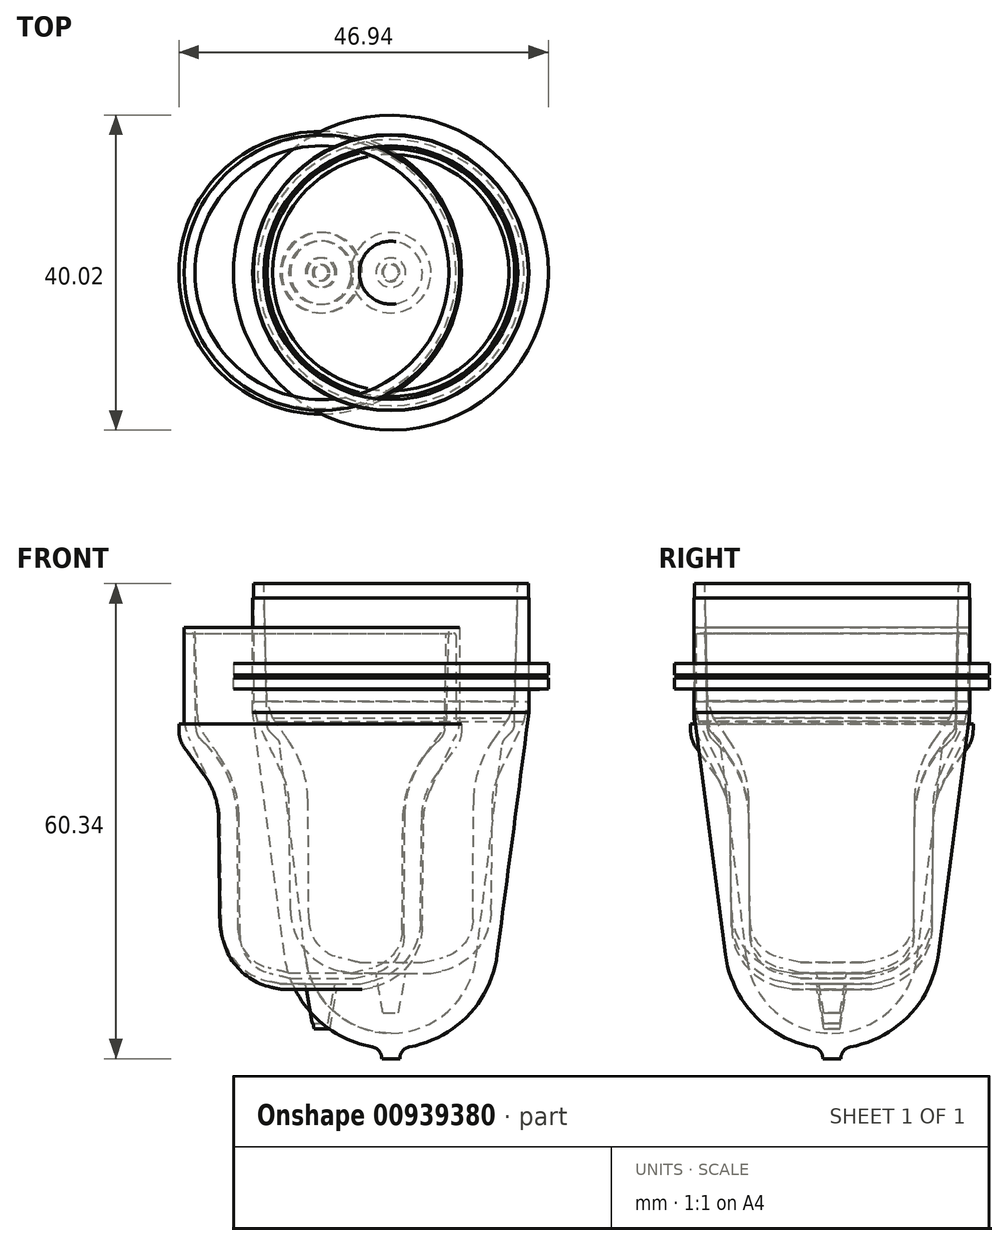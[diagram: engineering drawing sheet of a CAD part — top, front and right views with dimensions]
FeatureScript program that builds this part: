
annotation { "Feature Type Name" : "Feature", "Feature Type Description" : "" }
export const myFeature = defineFeature(function(context is Context, id is Id, definition is map)
    precondition{}
    {
        {
            var Q0;
            Q0=qCreatedBy(makeId("Front.planeOp"),FACE);
            var sketch = newSketch(context, id + "F0", { "sketchPlane" : qUnion([Q0])});
            skLineSegment(sketch, "E0", {"start": v(8.28, 24.33) * mm, "end": v(8.28, 13.23) * mm});
            skLineSegment(sketch, "E1", {"start": v(-7.98, -24.77) * mm, "end": v(-7.1, -19.77) * mm});
            skArc(sketch, "E2", {"start": v(-2.57, -19.48) * mm, "mid": v(1.95, -16.73) * mm, "end": v(3.77, -11.76) * mm});
            skArc(sketch, "E3", {"start": v(5.61, 6.52) * mm, "mid": v(4.38, 4.1) * mm, "end": v(3.94, 1.4) * mm});
            skLineSegment(sketch, "E4", {"start": v(8.98, 13.23) * mm, "end": v(8.98, 12.5) * mm});
            skArc(sketch, "E5", {"start": v(8.23, 10.18) * mm, "mid": v(8.78, 11.29) * mm, "end": v(8.97, 12.5) * mm});
            skLineSegment(sketch, "E6", {"start": v(8.23, 10.18) * mm, "end": v(5.61, 6.52) * mm});
            skLineSegment(sketch, "E7", {"start": v(3.94, 1.4) * mm, "end": v(3.77, -11.76) * mm});
            skLineSegment(sketch, "E8", {"start": v(-2.57, -19.48) * mm, "end": v(-3.98, -19.77) * mm});
            skLineSegment(sketch, "E9", {"start": v(-3.87, -19.75) * mm, "end": v(-3.98, -19.77) * mm});
            skArc(sketch, "E10", {"start": v(8.28, 24.47) * mm, "mid": v(8.2, 24.69) * mm, "end": v(7.98, 24.77) * mm});
            skLineSegment(sketch, "E11", {"start": v(7.98, 24.77) * mm, "end": v(7.33, 24.77) * mm});
            skLineSegment(sketch, "E12", {"start": v(7.03, 24.48) * mm, "end": v(6.82, 12.67) * mm});
            skArc(sketch, "E13", {"start": v(7.33, 24.77) * mm, "mid": v(7.12, 24.69) * mm, "end": v(7.03, 24.48) * mm});
            skLineSegment(sketch, "E14", {"start": v(8.28, 24.47) * mm, "end": v(8.28, 24.32) * mm});
            skLineSegment(sketch, "E15", {"start": v(-8.98, -18.38) * mm, "end": v(-4.98, -18.38) * mm});
            skLineSegment(sketch, "E16", {"start": v(-4.98, -18.38) * mm, "end": v(-2.33, -17.72) * mm});
            skLineSegment(sketch, "E17", {"start": v(6.22, 11.3) * mm, "end": v(5.61, 10.7) * mm});
            skArc(sketch, "E18", {"start": v(6.22, 11.3) * mm, "mid": v(6.66, 11.93) * mm, "end": v(6.82, 12.69) * mm});
            skArc(sketch, "E19", {"start": v(-2.35, -17.72) * mm, "mid": v(0.37, -15.96) * mm, "end": v(1.44, -12.9) * mm});
            skArc(sketch, "E20", {"start": v(5.61, 10.7) * mm, "mid": v(2.65, 6.38) * mm, "end": v(1.55, 1.25) * mm});
            skLineSegment(sketch, "E21", {"start": v(1.51, -1.38) * mm, "end": v(1.44, -12.9) * mm});
            skLineSegment(sketch, "E22", {"start": v(1.55, 1.25) * mm, "end": v(1.51, -1.38) * mm});
            skLineSegment(sketch, "E23", {"start": v(-3.87, -19.75) * mm, "end": v(-7.1, -19.77) * mm});
            skLineSegment(sketch, "E24", {"start": v(-7.98, -24.77) * mm, "end": v(-8.98, -24.77) * mm});
            skLineSegment(sketch, "E25", {"start": v(8.28, 13.23) * mm, "end": v(8.98, 13.23) * mm});
            skLineSegment(sketch, "E26", {"start": v(-8.98, -24.77) * mm, "end": v(-8.98, -18.38) * mm});
            skSolve(sketch);
        }
        {
            var Q0;
            {var subQ7=sQuery(id+"F0.wireOp",EDGE,"E0");Q0=makeQuery(id+"F0.imprint","IMPRINT",FACE,{"disambiguationData":[TD([[makeQuery(id+"F0.imprint","IMPRINT",EDGE,{"derivedFrom":subQ7}),-1.0]])]});}
            var Q1;
            Q1=sQuery(id+"F0.wireOp",EDGE,"E26");
            revolve(context, id + "F1", {"surfaceOperationType" : NewSurfaceOperationType.NEW, "entities" : qUnion([Q0]), "axis" : qUnion([Q1]), "revolveType" : RevolveType.FULL});
        }
        {
            var Q0;
            Q0=qCreatedBy(makeId("Front.planeOp"),FACE);
            var sketch = newSketch(context, id + "F2", { "sketchPlane" : qUnion([Q0])});
            skLineSegment(sketch, "E27", {"start": v(8.75, 25.5) * mm, "end": v(8.75, 14.5) * mm});
            skLineSegment(sketch, "E28", {"start": v(-7.75, -25.5) * mm, "end": v(-6.87, -20.5) * mm});
            skArc(sketch, "E29", {"start": v(-2.35, -20.2) * mm, "mid": v(2.18, -17.45) * mm, "end": v(4, -12.48) * mm});
            skLineSegment(sketch, "E30", {"start": v(8.75, 14.5) * mm, "end": v(8.75, 14.16) * mm});
            skLineSegment(sketch, "E31", {"start": v(4.17, 1.12) * mm, "end": v(4, -12.48) * mm});
            skLineSegment(sketch, "E32", {"start": v(-2.35, -20.2) * mm, "end": v(-3.75, -20.5) * mm});
            skLineSegment(sketch, "E33", {"start": v(-3.65, -20.48) * mm, "end": v(-3.75, -20.5) * mm});
            skLineSegment(sketch, "E34", {"start": v(-8.75, -19.1) * mm, "end": v(-4.75, -19.1) * mm});
            skLineSegment(sketch, "E35", {"start": v(-4.75, -19.1) * mm, "end": v(-2.1, -18.44) * mm});
            skArc(sketch, "E36", {"start": v(-2.12, -18.45) * mm, "mid": v(0.6, -16.69) * mm, "end": v(1.67, -13.63) * mm});
            skLineSegment(sketch, "E37", {"start": v(1.74, -2.1) * mm, "end": v(1.67, -13.63) * mm});
            skLineSegment(sketch, "E38", {"start": v(1.8, 1.53) * mm, "end": v(1.74, -2.1) * mm});
            skLineSegment(sketch, "E39", {"start": v(-3.65, -20.48) * mm, "end": v(-6.87, -20.5) * mm});
            skLineSegment(sketch, "E40", {"start": v(-7.75, -25.5) * mm, "end": v(-8.75, -25.5) * mm});
            skLineSegment(sketch, "E41", {"start": v(-8.75, -25.5) * mm, "end": v(-8.75, -19.1) * mm});
            skArc(sketch, "E42", {"start": v(5.01, 4.8) * mm, "mid": v(4.4, 3.01) * mm, "end": v(4.17, 1.12) * mm});
            skLineSegment(sketch, "E43", {"start": v(5.01, 4.8) * mm, "end": v(8.19, 11.62) * mm});
            skLineSegment(sketch, "E44", {"start": v(4.23, 9.07) * mm, "end": v(6.36, 12.1) * mm});
            skArc(sketch, "E45", {"start": v(8.19, 11.62) * mm, "mid": v(8.6, 12.86) * mm, "end": v(8.75, 14.16) * mm});
            skArc(sketch, "E46", {"start": v(4.23, 9.07) * mm, "mid": v(2.45, 5.49) * mm, "end": v(1.8, 1.53) * mm});
            skArc(sketch, "E47", {"start": v(6.36, 12.1) * mm, "mid": v(6.88, 13.15) * mm, "end": v(7.08, 14.3) * mm});
            skLineSegment(sketch, "E48", {"start": v(7.08, 14.3) * mm, "end": v(7.38, 25.5) * mm});
            skLineSegment(sketch, "E49", {"start": v(8.75, 25.5) * mm, "end": v(7.38, 25.5) * mm});
            skSolve(sketch);
        }
        {
            var Q0;
            Q0=makeQuery(id+"F2.imprint","IMPRINT",FACE,{"disambiguationData":[TD([[makeQuery(id+"F2.imprint","IMPRINT",EDGE,{"derivedFrom":sQuery(id+"F2.wireOp",EDGE,"E27")}),-1.0]])]});
            var Q1;
            Q1=sQuery(id+"F2.wireOp",EDGE,"E41");
            revolve(context, id + "F3", {"surfaceOperationType" : NewSurfaceOperationType.NEW, "entities" : qUnion([Q0]), "axis" : qUnion([Q1]), "revolveType" : RevolveType.FULL});
        }
        {
            var Q0;
            Q0=qCreatedBy(makeId("Front.planeOp"),FACE);
            var sketch = newSketch(context, id + "F4", { "sketchPlane" : qUnion([Q0])});
            skLineSegment(sketch, "E50", {"start": v(1, -23.46) * mm, "end": v(1.88, -18.46) * mm});
            skArc(sketch, "E51", {"start": v(6.4, -18.16) * mm, "mid": v(10.93, -15.41) * mm, "end": v(12.74, -10.44) * mm});
            skLineSegment(sketch, "E52", {"start": v(12.92, 3.16) * mm, "end": v(12.74, -10.44) * mm});
            skLineSegment(sketch, "E53", {"start": v(6.4, -18.16) * mm, "end": v(5, -18.46) * mm});
            skLineSegment(sketch, "E54", {"start": v(5.1, -18.44) * mm, "end": v(5, -18.46) * mm});
            skLineSegment(sketch, "E55", {"start": v(0, -17.06) * mm, "end": v(4, -17.06) * mm});
            skLineSegment(sketch, "E56", {"start": v(4, -17.06) * mm, "end": v(6.64, -16.4) * mm});
            skArc(sketch, "E57", {"start": v(6.63, -16.4) * mm, "mid": v(9.35, -14.65) * mm, "end": v(10.42, -11.59) * mm});
            skLineSegment(sketch, "E58", {"start": v(10.49, -0.06) * mm, "end": v(10.42, -11.59) * mm});
            skLineSegment(sketch, "E59", {"start": v(10.54, 3.57) * mm, "end": v(10.49, -0.06) * mm});
            skLineSegment(sketch, "E60", {"start": v(5.1, -18.44) * mm, "end": v(1.88, -18.46) * mm});
            skLineSegment(sketch, "E61", {"start": v(1, -23.46) * mm, "end": v(0, -23.46) * mm});
            skLineSegment(sketch, "E62", {"start": v(0, -23.46) * mm, "end": v(0, -17.06) * mm});
            skArc(sketch, "E63", {"start": v(13.76, 6.85) * mm, "mid": v(13.14, 5.05) * mm, "end": v(12.92, 3.16) * mm});
            skArc(sketch, "E64", {"start": v(12.98, 11.1) * mm, "mid": v(11.2, 7.52) * mm, "end": v(10.54, 3.57) * mm});
            skLineSegment(sketch, "E65", {"start": v(-1.16, -27.43) * mm, "end": v(-1.1, -27.43) * mm});
            skLineSegment(sketch, "E66", {"start": v(-1.1, -27.43) * mm, "end": v(-0.81, -27.43) * mm});
            skLineSegment(sketch, "E67", {"start": v(-0.81, -27.43) * mm, "end": v(-0.46, -27.43) * mm});
            skLineSegment(sketch, "E68", {"start": v(-0.46, -27.43) * mm, "end": v(-0.04, -27.43) * mm});
            skLineSegment(sketch, "E69", {"start": v(-0.04, -27.43) * mm, "end": v(0, -27.43) * mm});
            skLineSegment(sketch, "E70", {"start": v(-1.16, -27.36) * mm, "end": v(-1.16, -27.43) * mm});
            skLineSegment(sketch, "E71", {"start": v(-1.16, -27.36) * mm, "end": v(-1.16, -27.07) * mm});
            skLineSegment(sketch, "E72", {"start": v(-1.16, -27.07) * mm, "end": v(-1.3, -26.86) * mm});
            skLineSegment(sketch, "E73", {"start": v(-1.3, -26.86) * mm, "end": v(-1.38, -26.65) * mm});
            skLineSegment(sketch, "E74", {"start": v(-1.38, -26.65) * mm, "end": v(-1.59, -26.44) * mm});
            skLineSegment(sketch, "E75", {"start": v(-1.59, -26.44) * mm, "end": v(-1.73, -26.3) * mm});
            skLineSegment(sketch, "E76", {"start": v(-1.73, -26.3) * mm, "end": v(-1.94, -26.16) * mm});
            skLineSegment(sketch, "E77", {"start": v(-1.94, -26.16) * mm, "end": v(-2.15, -26.02) * mm});
            skLineSegment(sketch, "E78", {"start": v(-2.15, -26.02) * mm, "end": v(-2.43, -25.95) * mm});
            skLineSegment(sketch, "E79", {"start": v(-13.73, -14.23) * mm, "end": v(-13.23, -16.35) * mm});
            skLineSegment(sketch, "E80", {"start": v(-13.23, -16.35) * mm, "end": v(-12.46, -18.4) * mm});
            skLineSegment(sketch, "E81", {"start": v(-12.46, -18.4) * mm, "end": v(-11.4, -20.3) * mm});
            skLineSegment(sketch, "E82", {"start": v(-11.4, -20.3) * mm, "end": v(-9.99, -21.92) * mm});
            skLineSegment(sketch, "E83", {"start": v(-9.99, -21.92) * mm, "end": v(-8.36, -23.4) * mm});
            skLineSegment(sketch, "E84", {"start": v(-8.36, -23.4) * mm, "end": v(-6.53, -24.53) * mm});
            skLineSegment(sketch, "E85", {"start": v(-6.53, -24.53) * mm, "end": v(-4.55, -25.45) * mm});
            skLineSegment(sketch, "E86", {"start": v(-4.55, -25.45) * mm, "end": v(-2.43, -25.95) * mm});
            skLineSegment(sketch, "E87", {"start": v(-17.4, 13.79) * mm, "end": v(-13.73, -14.23) * mm});
            skLineSegment(sketch, "E88", {"start": v(-17.47, 15.27) * mm, "end": v(-17.47, 15.06) * mm});
            skLineSegment(sketch, "E89", {"start": v(-17.47, 15.06) * mm, "end": v(-17.47, 14.91) * mm});
            skLineSegment(sketch, "E90", {"start": v(-17.47, 14.91) * mm, "end": v(-17.47, 14.7) * mm});
            skLineSegment(sketch, "E91", {"start": v(-17.47, 14.7) * mm, "end": v(-17.47, 14.5) * mm});
            skLineSegment(sketch, "E92", {"start": v(-17.47, 14.5) * mm, "end": v(-17.4, 14.35) * mm});
            skLineSegment(sketch, "E93", {"start": v(-17.4, 14.35) * mm, "end": v(-17.4, 14.14) * mm});
            skLineSegment(sketch, "E94", {"start": v(-17.4, 14.14) * mm, "end": v(-17.4, 14) * mm});
            skLineSegment(sketch, "E95", {"start": v(-17.4, 14) * mm, "end": v(-17.4, 13.79) * mm});
            skLineSegment(sketch, "E96", {"start": v(-17.54, 16.54) * mm, "end": v(-17.47, 15.27) * mm});
            skLineSegment(sketch, "E97", {"start": v(-15.7, 14.91) * mm, "end": v(-16.12, 31.07) * mm});
            skLineSegment(sketch, "E98", {"start": v(-15.7, 14.91) * mm, "end": v(-15.7, 14.77) * mm});
            skLineSegment(sketch, "E99", {"start": v(-15.7, 14.77) * mm, "end": v(-15.7, 14.63) * mm});
            skLineSegment(sketch, "E100", {"start": v(-15.7, 14.63) * mm, "end": v(-15.63, 14.56) * mm});
            skLineSegment(sketch, "E101", {"start": v(-15.63, 14.56) * mm, "end": v(-15.63, 14.42) * mm});
            skLineSegment(sketch, "E102", {"start": v(-15.63, 14.42) * mm, "end": v(-15.56, 14.35) * mm});
            skLineSegment(sketch, "E103", {"start": v(-15.56, 14.35) * mm, "end": v(-15.49, 14.2) * mm});
            skLineSegment(sketch, "E104", {"start": v(-15.49, 14.2) * mm, "end": v(-15.42, 14.14) * mm});
            skLineSegment(sketch, "E105", {"start": v(-15.42, 14.14) * mm, "end": v(-15.35, 14.07) * mm});
            skLineSegment(sketch, "E106", {"start": v(-14.64, 13.36) * mm, "end": v(-15.35, 14.07) * mm});
            skLineSegment(sketch, "E107", {"start": v(-14.3, 12.59) * mm, "end": v(-14.3, 12.66) * mm});
            skLineSegment(sketch, "E108", {"start": v(-14.3, 12.66) * mm, "end": v(-14.3, 12.8) * mm});
            skLineSegment(sketch, "E109", {"start": v(-14.3, 12.8) * mm, "end": v(-14.36, 12.87) * mm});
            skLineSegment(sketch, "E110", {"start": v(-14.36, 12.87) * mm, "end": v(-14.43, 13) * mm});
            skLineSegment(sketch, "E111", {"start": v(-14.43, 13) * mm, "end": v(-14.43, 13.08) * mm});
            skLineSegment(sketch, "E112", {"start": v(-14.43, 13.08) * mm, "end": v(-14.5, 13.15) * mm});
            skLineSegment(sketch, "E113", {"start": v(-14.5, 13.15) * mm, "end": v(-14.57, 13.22) * mm});
            skLineSegment(sketch, "E114", {"start": v(-14.57, 13.22) * mm, "end": v(-14.64, 13.36) * mm});
            skLineSegment(sketch, "E115", {"start": v(-13.8, 8.5) * mm, "end": v(-14.3, 12.59) * mm});
            skLineSegment(sketch, "E116", {"start": v(-11.33, -11.7) * mm, "end": v(-11.54, -9.15) * mm});
            skLineSegment(sketch, "E117", {"start": v(-11.54, -9.15) * mm, "end": v(-11.82, -6.6) * mm});
            skLineSegment(sketch, "E118", {"start": v(-11.82, -6.6) * mm, "end": v(-12.1, -4.14) * mm});
            skLineSegment(sketch, "E119", {"start": v(-12.1, -4.14) * mm, "end": v(-12.38, -1.6) * mm});
            skLineSegment(sketch, "E120", {"start": v(-12.38, -1.6) * mm, "end": v(-12.74, 0.94) * mm});
            skLineSegment(sketch, "E121", {"start": v(-12.74, 0.94) * mm, "end": v(-13.02, 3.48) * mm});
            skLineSegment(sketch, "E122", {"start": v(-13.02, 3.48) * mm, "end": v(-13.37, 6.02) * mm});
            skLineSegment(sketch, "E123", {"start": v(-13.37, 6.02) * mm, "end": v(-13.8, 8.5) * mm});
            skLineSegment(sketch, "E124", {"start": v(-10.97, -14.58) * mm, "end": v(-11.33, -11.7) * mm});
            skLineSegment(sketch, "E125", {"start": v(-0.04, -24.25) * mm, "end": v(-2.01, -24.04) * mm});
            skLineSegment(sketch, "E126", {"start": v(-2.01, -24.04) * mm, "end": v(-3.92, -23.55) * mm});
            skLineSegment(sketch, "E127", {"start": v(-3.92, -23.55) * mm, "end": v(-5.75, -22.7) * mm});
            skLineSegment(sketch, "E128", {"start": v(-5.75, -22.7) * mm, "end": v(-7.3, -21.5) * mm});
            skLineSegment(sketch, "E129", {"start": v(-7.3, -21.5) * mm, "end": v(-8.72, -20.09) * mm});
            skLineSegment(sketch, "E130", {"start": v(-8.72, -20.09) * mm, "end": v(-9.77, -18.4) * mm});
            skLineSegment(sketch, "E131", {"start": v(-9.77, -18.4) * mm, "end": v(-10.55, -16.56) * mm});
            skLineSegment(sketch, "E132", {"start": v(-10.55, -16.56) * mm, "end": v(-10.97, -14.58) * mm});
            skLineSegment(sketch, "E133", {"start": v(16.12, 31.07) * mm, "end": v(15.74, 16.2) * mm});
            skLineSegment(sketch, "E134", {"start": v(15.74, 16.2) * mm, "end": v(15.01, 14) * mm});
            skLineSegment(sketch, "E135", {"start": v(15.01, 14) * mm, "end": v(12.98, 11.1) * mm});
            skLineSegment(sketch, "E136", {"start": v(17.47, 19.43) * mm, "end": v(17.47, 16.12) * mm});
            skLineSegment(sketch, "E137", {"start": v(17.47, 16.12) * mm, "end": v(16.9, 13.58) * mm});
            skLineSegment(sketch, "E138", {"start": v(16.9, 13.58) * mm, "end": v(13.76, 6.85) * mm});
            skLineSegment(sketch, "E139", {"start": v(20, 20.91) * mm, "end": v(17.47, 20.91) * mm});
            skLineSegment(sketch, "E140", {"start": v(17.47, 19.43) * mm, "end": v(20, 19.5) * mm});
            skLineSegment(sketch, "E141", {"start": v(20, 19.5) * mm, "end": v(20, 20.91) * mm});
            skLineSegment(sketch, "E142", {"start": v(-16.12, 31.07) * mm, "end": v(-16.83, 31.07) * mm});
            skLineSegment(sketch, "E143", {"start": v(-16.83, 31.07) * mm, "end": v(-17.32, 31.07) * mm});
            skLineSegment(sketch, "E144", {"start": v(-17.32, 31.07) * mm, "end": v(-17.54, 31.07) * mm});
            skLineSegment(sketch, "E145", {"start": v(17.47, 31.07) * mm, "end": v(17.32, 31.07) * mm});
            skLineSegment(sketch, "E146", {"start": v(17.32, 31.07) * mm, "end": v(16.76, 31.07) * mm});
            skLineSegment(sketch, "E147", {"start": v(16.76, 31.07) * mm, "end": v(16.12, 31.07) * mm});
            skLineSegment(sketch, "E148", {"start": v(17.47, 31.07) * mm, "end": v(17.47, 20.91) * mm});
            skLineSegment(sketch, "E149", {"start": v(-17.54, 16.54) * mm, "end": v(-17.54, 19.43) * mm});
            skLineSegment(sketch, "E150", {"start": v(-20, 19.5) * mm, "end": v(-17.54, 19.43) * mm});
            skLineSegment(sketch, "E151", {"start": v(-20, 20.91) * mm, "end": v(-20, 19.5) * mm});
            skLineSegment(sketch, "E152", {"start": v(-17.54, 20.91) * mm, "end": v(-20, 20.91) * mm});
            skLineSegment(sketch, "E153", {"start": v(-17.54, 20.91) * mm, "end": v(-17.54, 31.07) * mm});
            skLineSegment(sketch, "E154", {"start": v(-0.04, -24.25) * mm, "end": v(0, -24.25) * mm});
            skLineSegment(sketch, "E155", {"start": v(0, -24.68) * mm, "end": v(0, -24.68) * mm});
            skLineSegment(sketch, "E156", {"start": v(0, -31.07) * mm, "end": v(0, -24.68) * mm});
            skLineSegment(sketch, "E157", {"start": v(0, -26.51) * mm, "end": v(0, -26.51) * mm});
            skSolve(sketch);
        }
        {
            var Q0;
            Q0=makeQuery(id+"F4.imprint","IMPRINT",FACE,{"disambiguationData":[TD([[makeQuery(id+"F4.imprint","IMPRINT",EDGE,{"derivedFrom":sQuery(id+"F4.wireOp",EDGE,"E50")}),1.0]])]});
            var Q1;
            Q1=sQuery(id+"F4.wireOp",EDGE,"E62");
            revolve(context, id + "F5", {"surfaceOperationType" : NewSurfaceOperationType.NEW, "entities" : qUnion([Q0]), "axis" : qUnion([Q1]), "revolveType" : RevolveType.FULL});
        }
        {
            var Q0;
            Q0=qCreatedBy(makeId("Front.planeOp"),FACE);
            var sketch = newSketch(context, id + "F6", { "sketchPlane" : qUnion([Q0])});
            skLineSegment(sketch, "E158", {"start": v(1, -25.27) * mm, "end": v(1.88, -20.27) * mm});
            skArc(sketch, "E159", {"start": v(6.4, -19.97) * mm, "mid": v(10.93, -17.22) * mm, "end": v(12.74, -12.25) * mm});
            skLineSegment(sketch, "E160", {"start": v(12.92, 1.35) * mm, "end": v(12.74, -12.25) * mm});
            skLineSegment(sketch, "E161", {"start": v(6.4, -19.97) * mm, "end": v(5, -20.27) * mm});
            skLineSegment(sketch, "E162", {"start": v(5.1, -20.25) * mm, "end": v(5, -20.27) * mm});
            skLineSegment(sketch, "E163", {"start": v(0, -18.87) * mm, "end": v(4, -18.87) * mm});
            skLineSegment(sketch, "E164", {"start": v(4, -18.87) * mm, "end": v(6.64, -18.21) * mm});
            skArc(sketch, "E165", {"start": v(6.63, -18.21) * mm, "mid": v(9.35, -16.45) * mm, "end": v(10.42, -13.4) * mm});
            skLineSegment(sketch, "E166", {"start": v(10.49, -1.87) * mm, "end": v(10.42, -13.4) * mm});
            skLineSegment(sketch, "E167", {"start": v(10.54, 1.77) * mm, "end": v(10.49, -1.87) * mm});
            skLineSegment(sketch, "E168", {"start": v(5.1, -20.25) * mm, "end": v(1.88, -20.27) * mm});
            skLineSegment(sketch, "E169", {"start": v(1, -25.27) * mm, "end": v(0, -25.27) * mm});
            skLineSegment(sketch, "E170", {"start": v(0, -25.27) * mm, "end": v(0, -18.87) * mm});
            skArc(sketch, "E171", {"start": v(13.76, 5.04) * mm, "mid": v(13.14, 3.24) * mm, "end": v(12.92, 1.35) * mm});
            skArc(sketch, "E172", {"start": v(12.98, 9.3) * mm, "mid": v(11.2, 5.72) * mm, "end": v(10.54, 1.77) * mm});
            skLineSegment(sketch, "E173", {"start": v(-14.64, 11.56) * mm, "end": v(-15.35, 12.26) * mm});
            skLineSegment(sketch, "E174", {"start": v(16.12, 29.27) * mm, "end": v(15.74, 14.4) * mm});
            skLineSegment(sketch, "E175", {"start": v(15.74, 14.4) * mm, "end": v(15.01, 12.2) * mm});
            skLineSegment(sketch, "E176", {"start": v(15.01, 12.2) * mm, "end": v(12.98, 9.3) * mm});
            skLineSegment(sketch, "E177", {"start": v(17.47, 17.62) * mm, "end": v(17.47, 14.31) * mm});
            skLineSegment(sketch, "E178", {"start": v(17.47, 14.31) * mm, "end": v(16.9, 11.78) * mm});
            skLineSegment(sketch, "E179", {"start": v(16.9, 11.78) * mm, "end": v(13.76, 5.04) * mm});
            skLineSegment(sketch, "E180", {"start": v(20, 19.1) * mm, "end": v(17.47, 19.1) * mm});
            skLineSegment(sketch, "E181", {"start": v(17.47, 17.62) * mm, "end": v(20, 17.7) * mm});
            skLineSegment(sketch, "E182", {"start": v(20, 17.7) * mm, "end": v(20, 19.1) * mm});
            skLineSegment(sketch, "E183", {"start": v(-16.12, 29.27) * mm, "end": v(-16.83, 29.27) * mm});
            skLineSegment(sketch, "E184", {"start": v(-16.83, 29.27) * mm, "end": v(-17.32, 29.27) * mm});
            skLineSegment(sketch, "E185", {"start": v(-17.32, 29.27) * mm, "end": v(-17.54, 29.27) * mm});
            skLineSegment(sketch, "E186", {"start": v(17.47, 29.27) * mm, "end": v(17.32, 29.27) * mm});
            skLineSegment(sketch, "E187", {"start": v(17.32, 29.27) * mm, "end": v(16.76, 29.27) * mm});
            skLineSegment(sketch, "E188", {"start": v(16.76, 29.27) * mm, "end": v(16.12, 29.27) * mm});
            skLineSegment(sketch, "E189", {"start": v(17.47, 29.27) * mm, "end": v(17.47, 19.1) * mm});
            skLineSegment(sketch, "E190", {"start": v(-17.54, 14.73) * mm, "end": v(-17.54, 17.62) * mm});
            skLineSegment(sketch, "E191", {"start": v(-20, 17.7) * mm, "end": v(-17.54, 17.62) * mm});
            skLineSegment(sketch, "E192", {"start": v(-20, 19.1) * mm, "end": v(-20, 17.7) * mm});
            skLineSegment(sketch, "E193", {"start": v(-17.54, 19.1) * mm, "end": v(-20, 19.1) * mm});
            skLineSegment(sketch, "E194", {"start": v(-17.54, 19.1) * mm, "end": v(-17.54, 29.27) * mm});
            skLineSegment(sketch, "E195", {"start": v(0, -28.32) * mm, "end": v(0, -28.32) * mm});
            skLineSegment(sketch, "E196", {"start": v(-14.49, 11.4) * mm, "end": v(-15.33, 12.24) * mm});
            skLineSegment(sketch, "E197", {"start": v(-14.12, 10.65) * mm, "end": v(-10.84, -16.42) * mm});
            skArc(sketch, "E198", {"start": v(-14.12, 10.65) * mm, "mid": v(-14.24, 11.06) * mm, "end": v(-14.49, 11.4) * mm});
            skArc(sketch, "E199", {"start": v(-15.7, 13.1) * mm, "mid": v(-15.6, 12.64) * mm, "end": v(-15.33, 12.24) * mm});
            skLineSegment(sketch, "E200", {"start": v(-15.7, 13.1) * mm, "end": v(-16.12, 29.27) * mm});
            skArc(sketch, "E201", {"start": v(-10.84, -16.42) * mm, "mid": v(-7.24, -23.28) * mm, "end": v(0, -26.03) * mm});
            skArc(sketch, "E202", {"start": v(-13.51, -16.05) * mm, "mid": v(-9.85, -23.72) * mm, "end": v(-2.38, -27.77) * mm});
            skLineSegment(sketch, "E203", {"start": v(-13.51, -16.05) * mm, "end": v(-17.54, 14.73) * mm});
            skLineSegment(sketch, "E204", {"start": v(-1.14, -29.27) * mm, "end": v(0, -29.27) * mm});
            skLineSegment(sketch, "E205", {"start": v(-1.15, -29.11) * mm, "end": v(-1.14, -29.27) * mm});
            skArc(sketch, "E206", {"start": v(-1.15, -29.11) * mm, "mid": v(-1.54, -28.23) * mm, "end": v(-2.38, -27.77) * mm});
            skLineSegment(sketch, "E207", {"start": v(-17.54, 19.1) * mm, "end": v(-17.54, 17.62) * mm});
            skLineSegment(sketch, "E208", {"start": v(17.47, 19.1) * mm, "end": v(17.47, 17.62) * mm});
            skLineSegment(sketch, "E209", {"start": v(0, -26.03) * mm, "end": v(0, -29.27) * mm});
            skSolve(sketch);
        }
        {
            var Q0;
            Q0=makeQuery(id+"F6.imprint","IMPRINT",FACE,{"disambiguationData":[TD([[makeQuery(id+"F6.imprint","IMPRINT",EDGE,{"derivedFrom":sQuery(id+"F6.wireOp",EDGE,"E183")}),1.0]])]});
            var Q1;
            Q1=makeQuery(id+"F6.imprint","IMPRINT",FACE,{"disambiguationData":[TD([[makeQuery(id+"F6.imprint","IMPRINT",EDGE,{"derivedFrom":sQuery(id+"F6.wireOp",EDGE,"E191")}),1.0]])]});
            var Q2;
            Q2=sQuery(id+"F6.wireOp",EDGE,"E209");
            revolve(context, id + "F7", {"surfaceOperationType" : NewSurfaceOperationType.NEW, "entities" : qUnion([Q0, Q1]), "axis" : qUnion([Q2]), "revolveType" : RevolveType.FULL});
        }
    });
